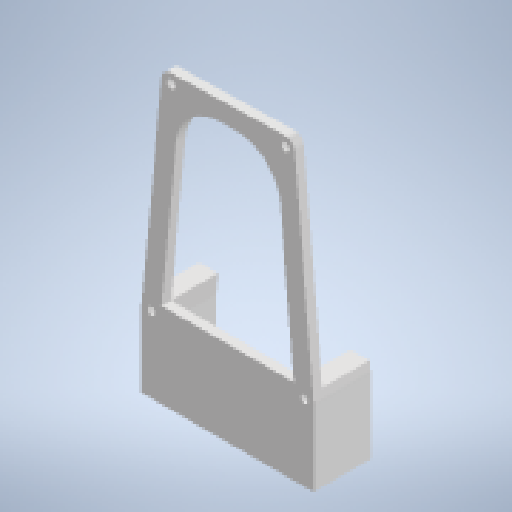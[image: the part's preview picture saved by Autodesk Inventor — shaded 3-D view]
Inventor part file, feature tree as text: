
AUTODESK INVENTOR PART (.ipt)
format: ipt  version: 2023 (Build 270158000, 158)  size: 368,640 bytes
history: native  units: mm
features: other x24, extrude x6, sketch x6, projected_geometry x5, fillet x1
ambient origin geometry x8: Origin, YZ Plane, XZ Plane, XY Plane, X Axis, Y Axis, Z Axis, Center Point
bodies: Solide1 (feature_tree)
feature tree (42):
  extrude  "Extrusion1"  Depth=8.0mm
  fillet  "Congé1"  Radius=8.0mm
  extrude  "Extrusion2"  Depth=8.0mm
  extrude  "Extrusion3"  Depth=8.0mm
  extrude  "Extrusion4"  Depth=4.0mm TaperAngle=0.0deg
  extrude  "Extrusion5"  Depth=19.0mm
  sketch  "Esquisse6"
  other  "Plan de construction1"
  extrude  "Extrusion6"  Depth=20.0mm TaperAngle=0.0deg
  sketch  "Esquisse1"
  other  "Référence1"
  other  "Référence2"
  other  "Référence3"
  other  "Référence4"
  other  "Référence5"
  sketch  "Esquisse2"
  projected_geometry  "Boucle projetée1"
  sketch  "Esquisse3"
  projected_geometry  "Boucle projetée2"
  projected_geometry  "Boucle projetée3"
  projected_geometry  "Boucle projetée4"
  sketch  "Esquisse4"
  projected_geometry  "Boucle projetée5"
  sketch  "Esquisse5"
  other  "Référence6"
  other  "Référence7"
  other  "Référence8"
  other  "Référence9"
  other  "Référence10"
  other  "Référence11"
  other  "Référence12"
  other  "Référence13"
  other  "Référence14"
  other  "Référence15"
  other  "<userpath>\Desktop\Robot\blocdrivermoteur.iam"
  other  "blocdrivermoteur.iam"
  other  "NUCLEO-F411RE:1"
  other  "xnucleo:1"
  other  "xucleobase:1"
  other  "<userpath>\Desktop\Robot\Robotbebou.iam"
  other  "Robotbebou.iam"
  other  "embase:1"
